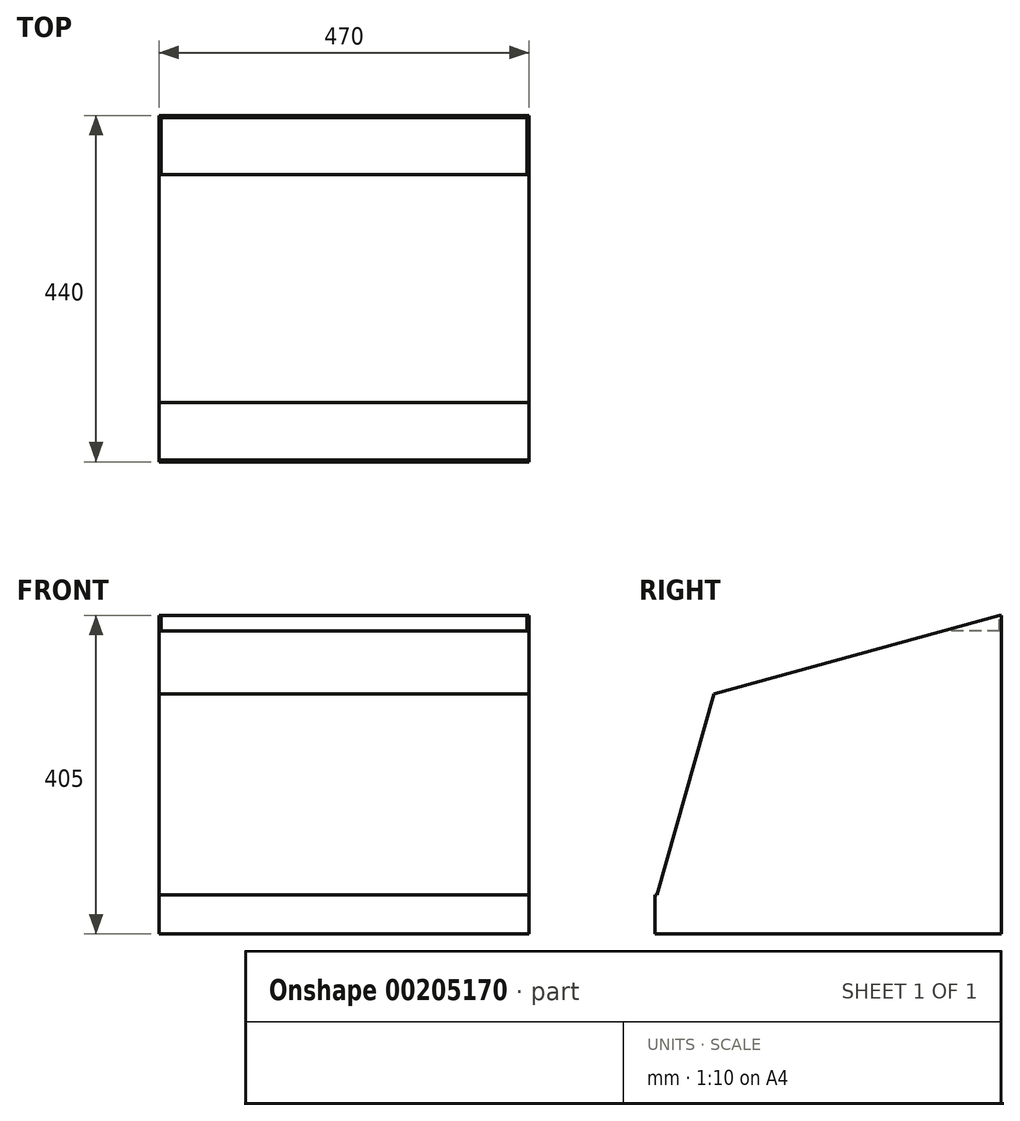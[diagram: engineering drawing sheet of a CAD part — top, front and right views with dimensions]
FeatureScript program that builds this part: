
annotation { "Feature Type Name" : "Feature", "Feature Type Description" : "" }
export const myFeature = defineFeature(function(context is Context, id is Id, definition is map)
    precondition{}
    {
        {
            var Q0;
            Q0=qCreatedBy(makeId("Top.planeOp"),FACE);
            var sketch = newSketch(context, id + "F0", { "sketchPlane" : qUnion([Q0])});
            skLineSegment(sketch, "E0.bottom", {"start": v(0, 0) * mm, "end": v(-470, 0) * mm});
            skLineSegment(sketch, "E0.top", {"start": v(0, -440) * mm, "end": v(-470, -440) * mm});
            skLineSegment(sketch, "E0.left", {"start": v(0, 0) * mm, "end": v(0, -440) * mm});
            skLineSegment(sketch, "E0.right", {"start": v(-470, 0) * mm, "end": v(-470, -440) * mm});
            skSolve(sketch);
        }
        {
            var Q0;
            Q0=qSketchRegion(id+"F0",true);
            extrude(context, id + "F1", {"entities" : qUnion([Q0]), "depth" : 405 * mm});
        }
        {
            var Q0;
            Q0=qCreatedBy(makeId("Right.planeOp"),FACE);
            var sketch = newSketch(context, id + "F2", { "sketchPlane" : qUnion([Q0])});
            skLineSegment(sketch, "E1.0.0", {"start": v(-440, 0) * mm, "end": v(0, 0) * mm, "construction": true});
            skLineSegment(sketch, "E1.0.1", {"start": v(0, 0) * mm, "end": v(0, 405) * mm, "construction": true});
            skLineSegment(sketch, "E2", {"start": v(-440, 0) * mm, "end": v(-440, 50) * mm, "construction": true});
            skLineSegment(sketch, "E3", {"start": v(-440, 50) * mm, "end": v(-437.5, 50) * mm});
            skLineSegment(sketch, "E4", {"start": v(0, 405) * mm, "end": v(-2.5, 405) * mm, "construction": true});
            skLineSegment(sketch, "E5", {"start": v(-365, 305) * mm, "end": v(-437.5, 50) * mm});
            skLineSegment(sketch, "E6", {"start": v(-365, 305) * mm, "end": v(-2.5, 405) * mm});
            skLineSegment(sketch, "E7.0", {"start": v(-2.5, 405) * mm, "end": v(-440, 405) * mm, "construction": true});
            skLineSegment(sketch, "E7.1", {"start": v(-440, 405) * mm, "end": v(-440, 0) * mm, "construction": true});
            skLineSegment(sketch, "E8", {"start": v(-440, 50) * mm, "end": v(-440, 405) * mm});
            skLineSegment(sketch, "E9", {"start": v(-2.5, 405) * mm, "end": v(-440, 405) * mm});
            skSolve(sketch);
        }
        {
            var Q0;
            Q0 = qSketchRegion(id + "F2", true);
            var Q1;
            Q1=makeQuery(id+"F1.opExtrude","SWEPT_FACE",FACE,{"disambiguationData":[OSD([sQuery(id+"F0.wireOp",EDGE,"E0.right")])]});
            extrude(context, id + "F3", {"entities" : qUnion([Q0]), "operationType" : NewBodyOperationType.REMOVE, "endBound" : BoundingType.UP_TO_SURFACE, "oppositeDirection" : true, "endBoundEntityFace" : qUnion([Q1]), "depth" : 25 * mm});
        }
        {
            var Q0;
            Q0=qCreatedBy(makeId("Top.planeOp"),FACE);
            cPlane(context, id + "F4", {"entities" : qUnion([Q0]), "cplaneType" : CPlaneType.OFFSET, "offset" : 410 * mm, "width" : 150 * mm, "height" : 150 * mm});
        }
        {
            var Q0;
            Q0=qCreatedBy(id+"F4.planeOp",FACE);
            var sketch = newSketch(context, id + "F5", { "sketchPlane" : qUnion([Q0])});
            skLineSegment(sketch, "E10.0", {"start": v(0, 0) * mm, "end": v(-470, 0) * mm, "construction": true});
            skLineSegment(sketch, "E11.0", {"start": v(0, -2.5) * mm, "end": v(-470, -2.5) * mm, "construction": true});
            skLineSegment(sketch, "E12", {"start": v(-470, 0) * mm, "end": v(-470, -2.5) * mm});
            skLineSegment(sketch, "E13.0", {"start": v(-467.5, 0) * mm, "end": v(-467.5, -2.5) * mm});
            skLineSegment(sketch, "E14", {"start": v(0, -2.5) * mm, "end": v(0, 0) * mm});
            skLineSegment(sketch, "E15.0", {"start": v(-2.5, -2.5) * mm, "end": v(-2.5, 0) * mm});
            skLineSegment(sketch, "E16.0", {"start": v(-470, -440) * mm, "end": v(0, -440) * mm, "construction": true});
            skLineSegment(sketch, "E17.0", {"start": v(-470, -437.5) * mm, "end": v(0, -437.5) * mm, "construction": true});
            skLineSegment(sketch, "E18.bottom", {"start": v(-2.5, -2.5) * mm, "end": v(-467.5, -2.5) * mm});
            skLineSegment(sketch, "E18.top", {"start": v(-2.5, -437.5) * mm, "end": v(-467.5, -437.5) * mm});
            skLineSegment(sketch, "E18.left", {"start": v(-2.5, -2.5) * mm, "end": v(-2.5, -437.5) * mm});
            skLineSegment(sketch, "E18.right", {"start": v(-467.5, -2.5) * mm, "end": v(-467.5, -437.5) * mm});
            skSolve(sketch);
        }
        {
            var Q0;
            Q0=makeQuery(id+"F5.imprint","IMPRINT",FACE,{"disambiguationData":[TD([[makeQuery(id+"F5.imprint","IMPRINT",EDGE,{"derivedFrom":sQuery(id+"F5.wireOp",EDGE,"E18.bottom")}),1.0]])]});
            extrude(context, id + "F6", {"entities" : qUnion([Q0]), "operationType" : NewBodyOperationType.REMOVE, "oppositeDirection" : true, "depth" : 25 * mm});
        }
    });
